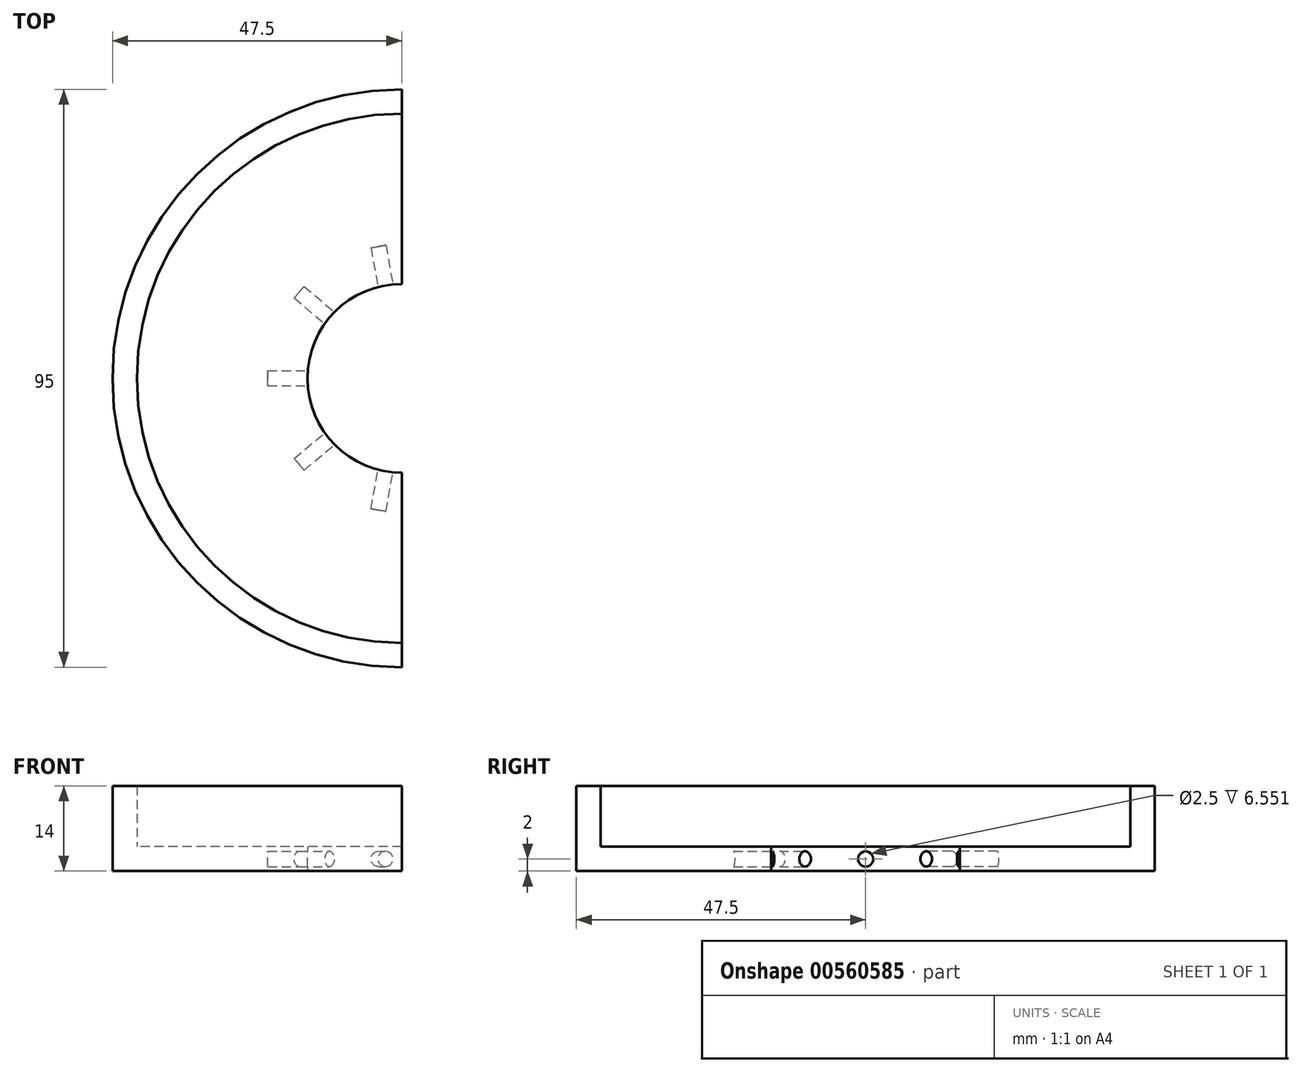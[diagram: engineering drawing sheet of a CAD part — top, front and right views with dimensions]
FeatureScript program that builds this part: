
annotation { "Feature Type Name" : "Feature", "Feature Type Description" : "" }
export const myFeature = defineFeature(function(context is Context, id is Id, definition is map)
    precondition{}
    {
        {
            var Q0;
            Q0=qCreatedBy(makeId("Top.planeOp"),FACE);
            var sketch = newSketch(context, id + "F0", { "sketchPlane" : qUnion([Q0])});
            skArc(sketch, "E0", {"start": v(0, -47.5) * mm, "mid": v(-47.5, 0) * mm, "end": v(0, 47.5) * mm});
            skArc(sketch, "E1", {"start": v(0, -15.5) * mm, "mid": v(-15.5, 0) * mm, "end": v(0, 15.5) * mm});
            skLineSegment(sketch, "E2", {"start": v(0, 47.5) * mm, "end": v(0, 15.5) * mm});
            skLineSegment(sketch, "E3", {"start": v(0, -15.5) * mm, "end": v(0, -47.5) * mm});
            skLineSegment(sketch, "E4", {"start": v(0, 0) * mm, "end": v(-58.9, 0) * mm, "construction": true});
            skSolve(sketch);
        }
        {
            var Q0;
            Q0 = qSketchRegion(id + "F0", true);
            extrude(context, id + "F1", {"entities" : qUnion([Q0]), "depth" : 4 * mm, "offsetDistance" : 25 * mm});
        }
        {
            var Q0;
            Q0=makeQuery(id+"F1.opExtrude","CAP_FACE",FACE,{"disambiguationData":[OSD([sQuery(id+"F0.wireOp",EDGE,"E0"),sQuery(id+"F0.wireOp",EDGE,"E1"),sQuery(id+"F0.wireOp",EDGE,"E2"),sQuery(id+"F0.wireOp",EDGE,"E3")])],"isStart":false});
            var sketch = newSketch(context, id + "F2", { "sketchPlane" : qUnion([Q0])});
            skArc(sketch, "E5", {"start": v(0, -43.5) * mm, "mid": v(-43.5, 0) * mm, "end": v(0, 43.5) * mm});
            skArc(sketch, "E6", {"start": v(0, -47.5) * mm, "mid": v(-47.5, 0) * mm, "end": v(0, 47.5) * mm});
            skLineSegment(sketch, "E7", {"start": v(0, 47.5) * mm, "end": v(0, 43.5) * mm});
            skLineSegment(sketch, "E8", {"start": v(0, -43.5) * mm, "end": v(0, -47.5) * mm});
            skSolve(sketch);
        }
        {
            var Q0;
            Q0 = qSketchRegion(id + "F2", true);
            extrude(context, id + "F3", {"entities" : qUnion([Q0]), "operationType" : NewBodyOperationType.ADD, "depth" : 10 * mm, "offsetDistance" : 25 * mm});
        }
        {
            var Q0;
            Q0=qCreatedBy(makeId("Right.planeOp"),FACE);
            var sketch = newSketch(context, id + "F4", { "sketchPlane" : qUnion([Q0])});
            skCircle(sketch, "E9", {"center": v(0, 2) * mm, "radius": 1.25 * mm});
            skSolve(sketch);
        }
        {
            var Q0;
            Q0 = qSketchRegion(id + "F4", true);
            extrude(context, id + "F5", {"entities" : qUnion([Q0]), "oppositeDirection" : true, "depth" : 22 * mm, "offsetDistance" : 25 * mm});
        }
        {
            var Q0;
            Q0=qCreatedBy(makeId("Right.planeOp"),FACE);
            var sketch = newSketch(context, id + "F6", { "sketchPlane" : qUnion([Q0])});
            skLineSegment(sketch, "E10", {"start": v(0, -5.02) * mm, "end": v(0, 25.41) * mm});
            skSolve(sketch);
        }
        {
            var Q0;
            Q0=makeQuery(id+"F5.opExtrude","SWEPT_BODY",BODY,{"disambiguationData":[OSD([sQuery(id+"F4.wireOp",EDGE,"E9")])]});
            var Q1;
            Q1=sQuery(id+"F6.wireOp",EDGE,"E10");
            circularPattern(context, id + "F7", {"operationType" : NewBodyOperationType.REMOVE, "entities" : qUnion([Q0]), "axis" : qUnion([Q1]), "angle" : 80 * degree, "instanceCount" : 3, "equalSpace" : true, "isCentered" : true});
        }
    });
